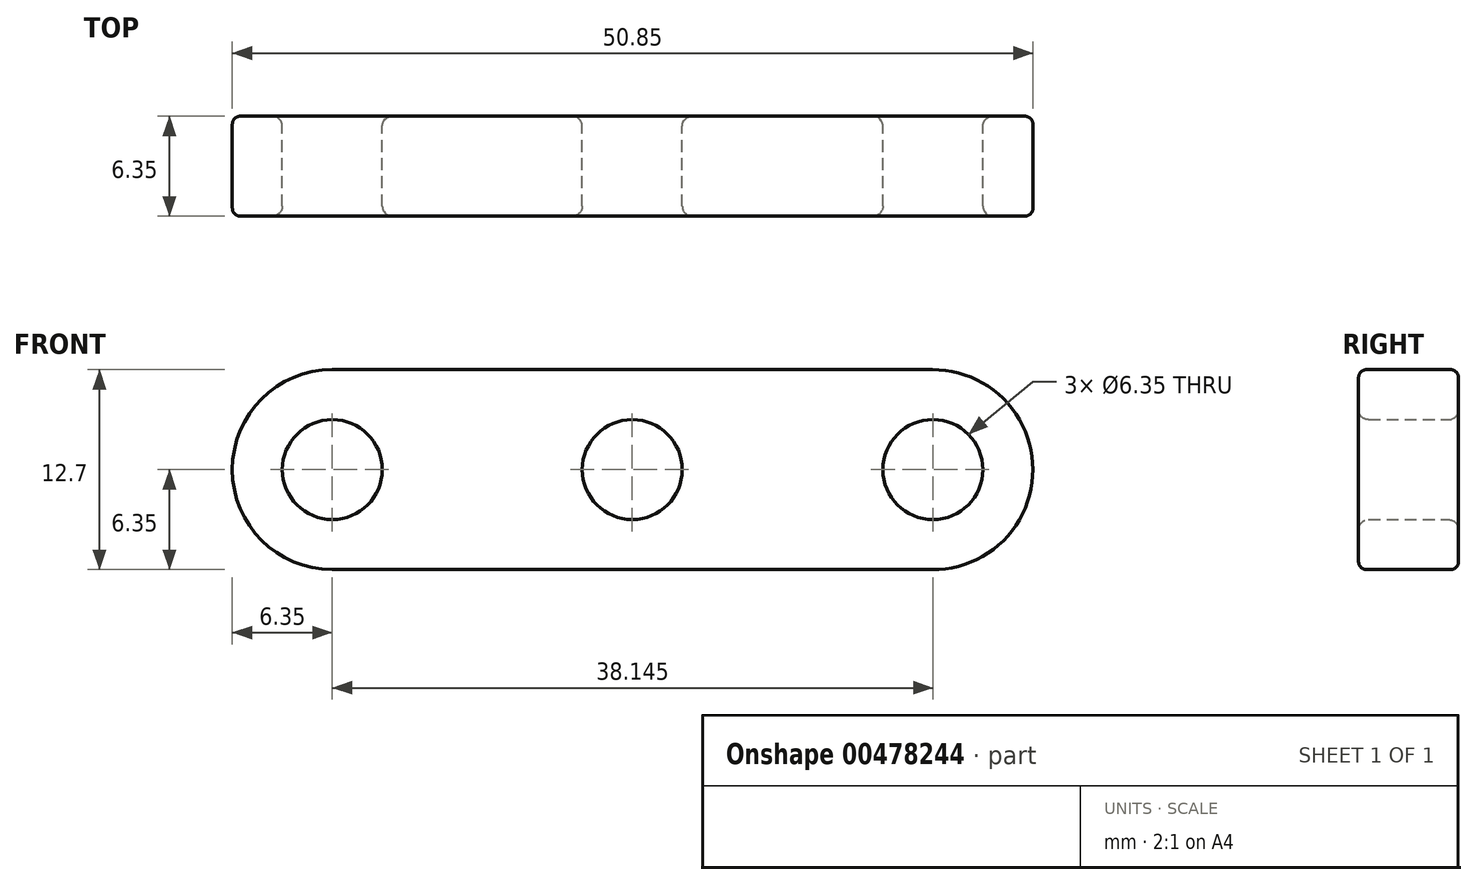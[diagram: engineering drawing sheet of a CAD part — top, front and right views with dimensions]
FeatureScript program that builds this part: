
annotation { "Feature Type Name" : "Feature", "Feature Type Description" : "" }
export const myFeature = defineFeature(function(context is Context, id is Id, definition is map)
    precondition{}
    {
        {
            var Q0;
            Q0=qCreatedBy(makeId("Front.planeOp"),FACE);
            var sketch = newSketch(context, id + "F0", { "sketchPlane" : qUnion([Q0])});
            skLineSegment(sketch, "E0.bottom", {"start": v(-19.05, 6.35) * mm, "end": v(19.05, 6.35) * mm});
            skLineSegment(sketch, "E0.top", {"start": v(-19.05, -6.35) * mm, "end": v(19.05, -6.35) * mm});
            skPoint(sketch, "E0.middle", {"position": v(0, 0) * mm});
            skArc(sketch, "E1", {"start": v(-19.05, 6.35) * mm, "mid": v(-25.4, 0) * mm, "end": v(-19.05, -6.35) * mm});
            skArc(sketch, "E2", {"start": v(19.05, -6.35) * mm, "mid": v(25.45, 0) * mm, "end": v(19.04, 6.35) * mm});
            skCircle(sketch, "E3", {"center": v(-19.05, 0) * mm, "radius": 3.18 * mm});
            skCircle(sketch, "E4", {"center": v(0, 0) * mm, "radius": 3.18 * mm});
            skCircle(sketch, "E5", {"center": v(19.1, 0) * mm, "radius": 3.18 * mm});
            skSolve(sketch);
        }
        {
            var Q0;
            {var subQ1=sQuery(id+"F0.wireOp",EDGE,"E0.bottom");Q0=makeQuery(id+"F0.imprint","IMPRINT",FACE,{"disambiguationData":[TD([[makeQuery(id+"F0.imprint","IMPRINT",EDGE,{"derivedFrom":subQ1}),-1.0]])]});}
            extrude(context, id + "F1", {"entities" : qUnion([Q0]), "depth" : 6.35 * mm});
        }
        {
            var Q0;
            Q0=makeQuery(id+"F1.opExtrude","CAP_EDGE",EDGE,{"disambiguationData":[OSD([sQuery(id+"F0.wireOp",EDGE,"E3")])],"isStart":false});
            var Q1;
            Q1=makeQuery(id+"F1.opExtrude","CAP_EDGE",EDGE,{"disambiguationData":[OSD([sQuery(id+"F0.wireOp",EDGE,"E4")])],"isStart":false});
            var Q2;
            Q2=makeQuery(id+"F1.opExtrude","CAP_EDGE",EDGE,{"disambiguationData":[OSD([sQuery(id+"F0.wireOp",EDGE,"E5")])],"isStart":false});
            var Q3;
            Q3=makeQuery(id+"F1.opExtrude","CAP_EDGE",EDGE,{"disambiguationData":[OSD([sQuery(id+"F0.wireOp",EDGE,"E5")])],"isStart":true});
            var Q4;
            Q4=makeQuery(id+"F1.opExtrude","CAP_EDGE",EDGE,{"disambiguationData":[OSD([sQuery(id+"F0.wireOp",EDGE,"E4")])],"isStart":true});
            var Q5;
            Q5=makeQuery(id+"F1.opExtrude","CAP_EDGE",EDGE,{"disambiguationData":[OSD([sQuery(id+"F0.wireOp",EDGE,"E3")])],"isStart":true});
            fillet(context, id + "F2", {"entities" : qUnion([Q0, Q1, Q2, Q3, Q4, Q5]), "radius" : 0.64 * mm, "tangentPropagation" : true, "allowEdgeOverflow" : false});
        }
        {
            var Q0;
            Q0=makeQuery(id+"F1.opExtrude","CAP_FACE",FACE,{"disambiguationData":[OSD([sQuery(id+"F0.wireOp",EDGE,"E0.bottom"),sQuery(id+"F0.wireOp",EDGE,"E0.top"),sQuery(id+"F0.wireOp",EDGE,"E1"),sQuery(id+"F0.wireOp",EDGE,"E2"),sQuery(id+"F0.wireOp",EDGE,"E3"),sQuery(id+"F0.wireOp",EDGE,"E4"),sQuery(id+"F0.wireOp",EDGE,"E5")])],"isStart":false});
            fillet(context, id + "F3", {"entities" : qUnion([Q0]), "radius" : 0.5 * mm, "tangentPropagation" : true, "allowEdgeOverflow" : false});
        }
        {
            var Q0;
            Q0=makeQuery(id+"F1.opExtrude","CAP_FACE",FACE,{"disambiguationData":[OSD([sQuery(id+"F0.wireOp",EDGE,"E0.bottom"),sQuery(id+"F0.wireOp",EDGE,"E0.top"),sQuery(id+"F0.wireOp",EDGE,"E1"),sQuery(id+"F0.wireOp",EDGE,"E2"),sQuery(id+"F0.wireOp",EDGE,"E3"),sQuery(id+"F0.wireOp",EDGE,"E4"),sQuery(id+"F0.wireOp",EDGE,"E5")])],"isStart":true});
            fillet(context, id + "F4", {"entities" : qUnion([Q0]), "radius" : 0.5 * mm, "tangentPropagation" : true, "allowEdgeOverflow" : false});
        }
    });
